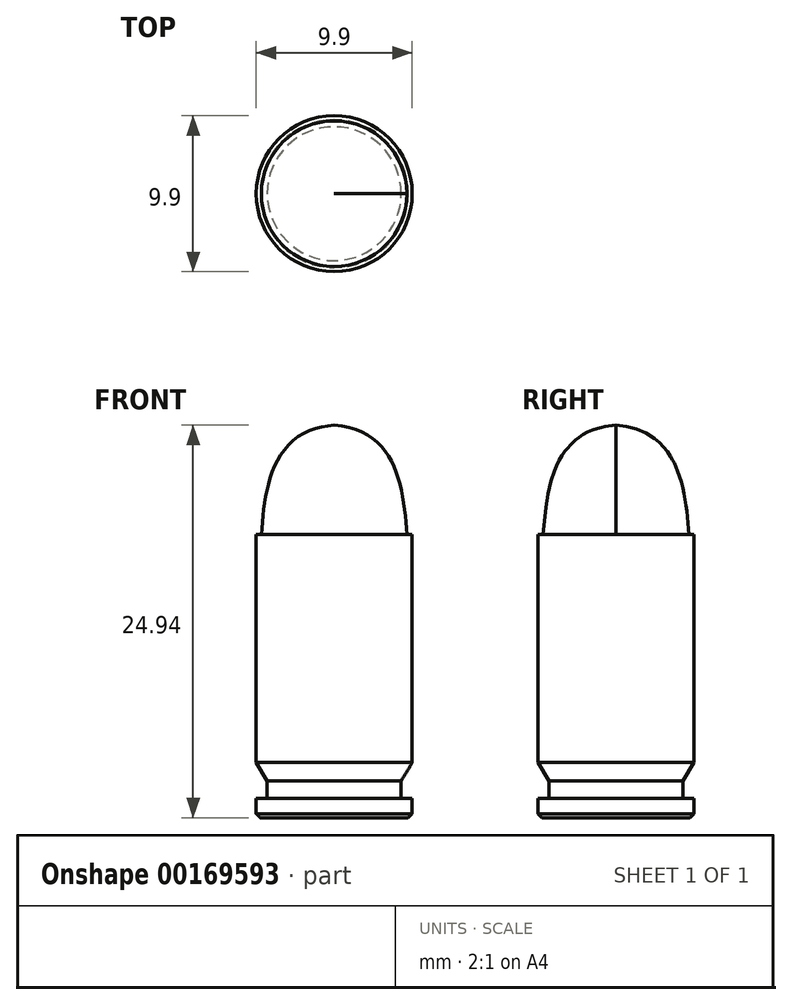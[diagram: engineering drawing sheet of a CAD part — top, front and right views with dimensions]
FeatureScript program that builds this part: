
annotation { "Feature Type Name" : "Feature", "Feature Type Description" : "" }
export const myFeature = defineFeature(function(context is Context, id is Id, definition is map)
    precondition{}
    {
        {
            var Q0;
            Q0=qCreatedBy(makeId("Front.planeOp"),FACE);
            var sketch = newSketch(context, id + "F0", { "sketchPlane" : qUnion([Q0])});
            skLineSegment(sketch, "E0.bottom", {"start": v(4.95, -7.24) * mm, "end": v(-4.95, -7.24) * mm});
            skLineSegment(sketch, "E0.top", {"start": v(4.95, 7.24) * mm, "end": v(-4.95, 7.24) * mm});
            skLineSegment(sketch, "E0.left", {"start": v(4.95, -7.24) * mm, "end": v(4.95, 7.24) * mm});
            skLineSegment(sketch, "E0.right", {"start": v(-4.95, -7.24) * mm, "end": v(-4.95, 7.24) * mm});
            skPoint(sketch, "E0.middle", {"position": v(0, 0) * mm});
            skLineSegment(sketch, "E1", {"start": v(-4.25, -8.4) * mm, "end": v(4.25, -8.4) * mm});
            skLineSegment(sketch, "E2.bottom", {"start": v(4.95, -10.74) * mm, "end": v(-4.95, -10.74) * mm});
            skLineSegment(sketch, "E2.top", {"start": v(4.95, -9.5) * mm, "end": v(-4.95, -9.5) * mm});
            skLineSegment(sketch, "E2.left", {"start": v(4.95, -10.74) * mm, "end": v(4.95, -9.5) * mm});
            skLineSegment(sketch, "E2.right", {"start": v(-4.95, -10.74) * mm, "end": v(-4.95, -9.5) * mm});
            skPoint(sketch, "E2.middle", {"position": v(0, -10.12) * mm});
            skLineSegment(sketch, "E3", {"start": v(-4.25, -8.4) * mm, "end": v(-4.25, -9.5) * mm});
            skLineSegment(sketch, "E4", {"start": v(4.25, -8.4) * mm, "end": v(4.25, -9.5) * mm});
            skPoint(sketch, "E5", {"position": v(0, -8.4) * mm});
            skLineSegment(sketch, "E6", {"start": v(-4.25, -8.4) * mm, "end": v(-4.95, -7.24) * mm});
            skLineSegment(sketch, "E7", {"start": v(4.25, -8.4) * mm, "end": v(4.95, -7.24) * mm});
            skLineSegment(sketch, "E8", {"start": v(0, 7.24) * mm, "end": v(0, 14.2) * mm});
            skFitSpline(sketch, "E9", {"points": [v(0, 14.2) * mm, v(4.62, 7.24) * mm], "startDerivative": vector(11.86, -0.86) * mm, "endDerivative": vector(0.63, -9.05) * mm});
            skFitSpline(sketch, "E10.MirrorCS", {"points": [v(0, 14.2) * mm, v(-4.62, 7.24) * mm], "startDerivative": vector(-11.86, -0.86) * mm, "endDerivative": vector(-0.63, -9.05) * mm});
            skLineSegment(sketch, "E11", {"start": v(0, 7.24) * mm, "end": v(0, -7.24) * mm});
            skLineSegment(sketch, "E12", {"start": v(0, -7.24) * mm, "end": v(0, -8.4) * mm});
            skLineSegment(sketch, "E13", {"start": v(0, -9.5) * mm, "end": v(0, -10.74) * mm});
            skLineSegment(sketch, "E14", {"start": v(0, -8.4) * mm, "end": v(0, -9.5) * mm});
            skSolve(sketch);
        }
        {
            var Q0;
            {var subQ0=sQuery(id+"F0.wireOp",EDGE,"E8");Q0=makeQuery(id+"F0.imprint","IMPRINT",FACE,{"disambiguationData":[TD([[makeQuery(id+"F0.imprint","IMPRINT",EDGE,{"derivedFrom":subQ0}),-1.0]])]});}
            var Q1;
            {var subQ0=sQuery(id+"F0.wireOp",EDGE,"E0.left");Q1=makeQuery(id+"F0.imprint","IMPRINT",FACE,{"disambiguationData":[TD([[makeQuery(id+"F0.imprint","IMPRINT",EDGE,{"derivedFrom":subQ0}),1.0]])]});}
            var Q2;
            {var subQ0=sQuery(id+"F0.wireOp",EDGE,"E7");Q2=makeQuery(id+"F0.imprint","IMPRINT",FACE,{"disambiguationData":[TD([[makeQuery(id+"F0.imprint","IMPRINT",EDGE,{"derivedFrom":subQ0}),1.0]])]});}
            var Q3;
            {var subQ0=sQuery(id+"F0.wireOp",EDGE,"E4");Q3=makeQuery(id+"F0.imprint","IMPRINT",FACE,{"disambiguationData":[TD([[makeQuery(id+"F0.imprint","IMPRINT",EDGE,{"derivedFrom":subQ0}),-1.0]])]});}
            var Q4;
            {var subQ0=sQuery(id+"F0.wireOp",EDGE,"E2.left");Q4=makeQuery(id+"F0.imprint","IMPRINT",FACE,{"disambiguationData":[TD([[makeQuery(id+"F0.imprint","IMPRINT",EDGE,{"derivedFrom":subQ0}),1.0]])]});}
            var Q5;
            Q5=sQuery(id+"F0.wireOp",EDGE,"E11");
            revolve(context, id + "F1", {"entities" : qUnion([Q0, Q1, Q2, Q3, Q4]), "axis" : qUnion([Q5]), "revolveType" : RevolveType.FULL});
        }
        {
            var Q0;
            Q0=makeQuery(id+"F1.opRevolve","SWEPT_EDGE",EDGE,{"disambiguationData":[OSD([sQuery(id+"F0.wireOp",EDGE,"E2.bottom"),sQuery(id+"F0.wireOp",EDGE,"E2.left")])]});
            chamfer(context, id + "F2", {"entities" : qUnion([Q0]), "width" : 0.25 * mm, "tangentPropagation" : true});
        }
    });
